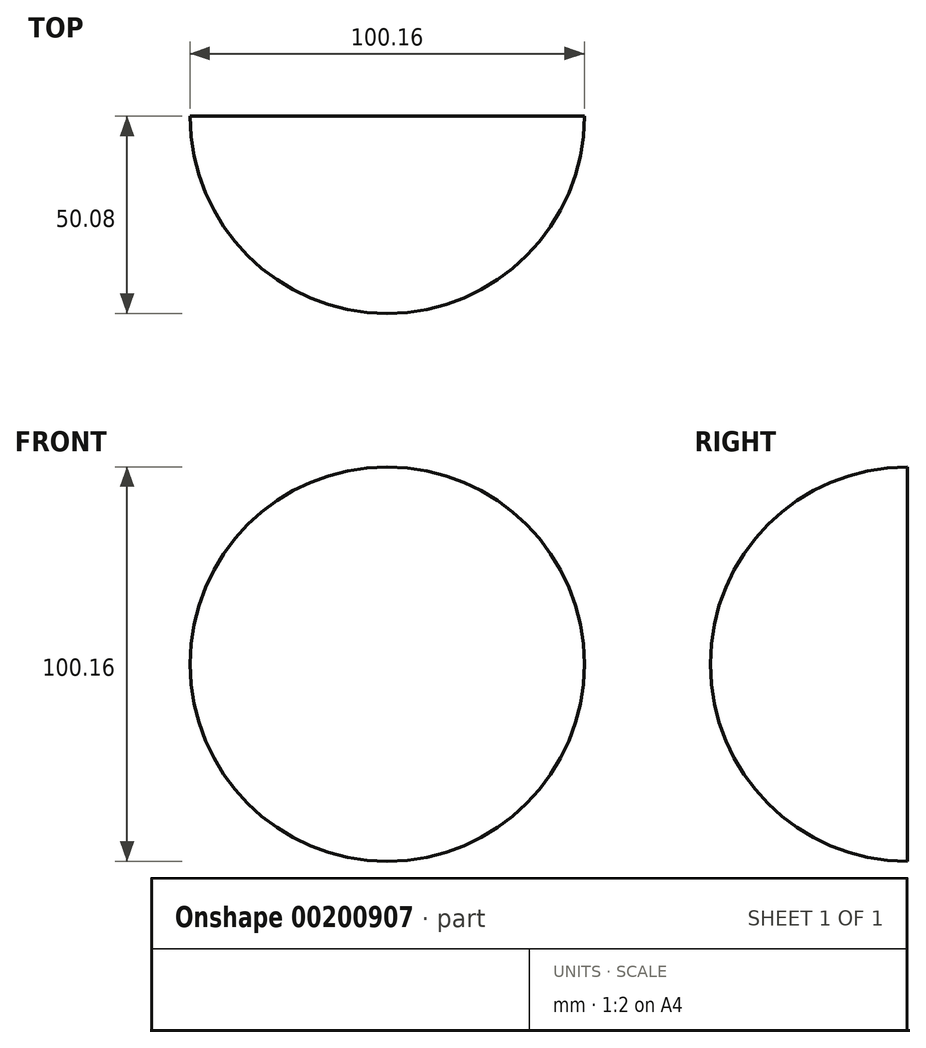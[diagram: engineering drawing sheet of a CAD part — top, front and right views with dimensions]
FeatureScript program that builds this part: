
annotation { "Feature Type Name" : "Feature", "Feature Type Description" : "" }
export const myFeature = defineFeature(function(context is Context, id is Id, definition is map)
    precondition{}
    {
        {
            var Q0;
            Q0=qCreatedBy(makeId("Right.planeOp"),FACE);
            var sketch = newSketch(context, id + "F0", { "sketchPlane" : qUnion([Q0])});
            skArc(sketch, "E0", {"start": v(-50.08, 0) * mm, "mid": v(-35.41, 35.41) * mm, "end": v(0, 50.08) * mm});
            skArc(sketch, "E1", {"start": v(-50.08, 0) * mm, "mid": v(-35.41, -35.41) * mm, "end": v(0, -50.08) * mm});
            skLineSegment(sketch, "E2", {"start": v(0, 50.08) * mm, "end": v(0, -50.08) * mm});
            skSolve(sketch);
        }
        {
            var Q0;
            Q0 = qSketchRegion(id + "F0", true);
            var Q1;
            Q1=sQuery(id+"F0.wireOp",EDGE,"E2");
            revolve(context, id + "F1", {"entities" : qUnion([Q0]), "axis" : qUnion([Q1]), "revolveType" : RevolveType.SYMMETRIC, "angle" : 180 * degree});
        }
    });
